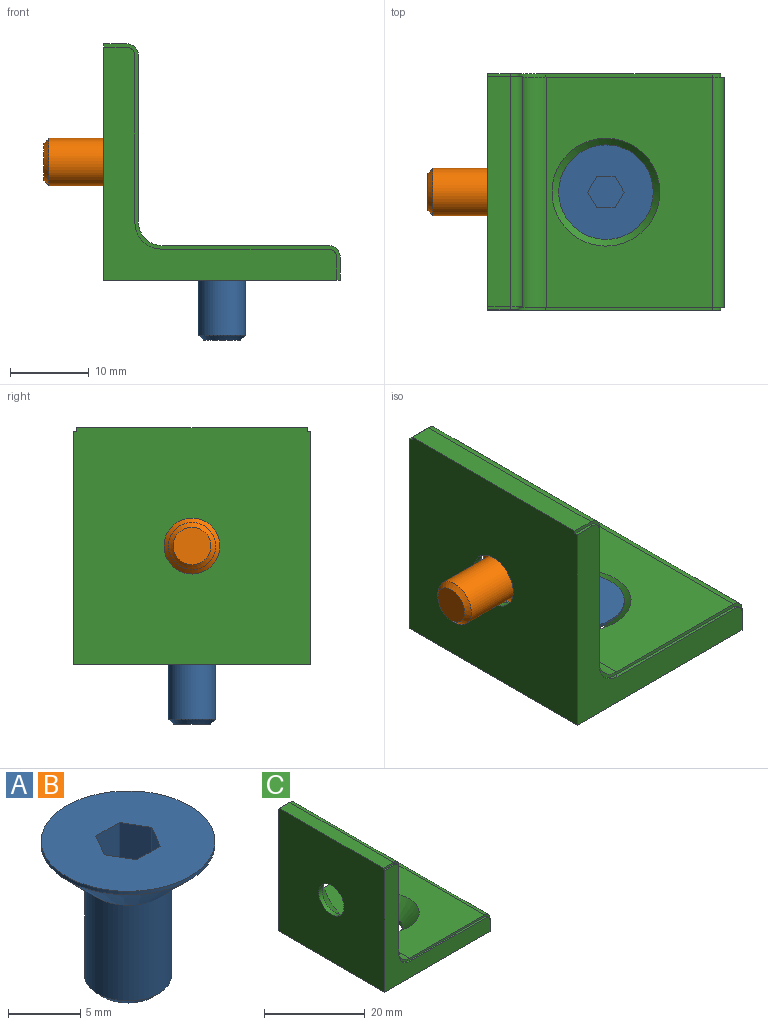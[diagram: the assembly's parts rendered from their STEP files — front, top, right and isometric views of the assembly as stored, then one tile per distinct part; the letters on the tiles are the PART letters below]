
ASSEMBLY  parts=3 mates=2
PART A: 13 faces, bbox 12x12x12 mm
  f0: cylinder r=6mm len=12mm, axis (0,0,-1), area 11.3mm2, adj f1,f9
  f1: cone r=3mm half-angle=45deg, axis (0,0,1), area 120mm2, adj f0,f2
  f2: cylinder r=3mm len=8.09mm, axis (0,0,-1), area 152.4mm2, adj f1,f3
  f3: cone r=1.5mm half-angle=45deg, axis (0,0,1), area 14.7mm2, adj f2,f12
  f4: plane 3.83x2mm, normal (0.87,0.5,0), area 8.9mm2, adj f6,f8,f9,f11
  f5: plane 3.83x2mm, normal (-0.87,-0.5,0), area 8.9mm2, adj f6,f7,f9,f10
  f6: plane 4.62x4mm, normal (0,0,1), area 13.9mm2, adj f4,f5,f7,f8,f10,f11
  f7: plane 3.83x2mm, normal (-0.87,0.5,0), area 8.9mm2, adj f5,f6,f9,f11
  f8: plane 3.83x2mm, normal (0.87,-0.5,0), area 8.9mm2, adj f4,f6,f9,f10
  f9: plane 12x12mm, normal (0,0,1), area 99.2mm2, adj f0,f4,f5,f7,f8,f10,f11
  f10: plane 3.83x2.31mm, normal (0,-1,0), area 8.9mm2, adj f5,f6,f8,f9
  f11: plane 3.83x2.31mm, normal (0,1,0), area 8.9mm2, adj f4,f6,f7,f9
  f12: plane 4.77x4.77mm, normal (0,0,-1), area 17.9mm2, adj f3
PART B: same geometry as A
PART C: 31 faces, bbox 30x30x30 mm
  f0: cone r=5.2mm half-angle=44.1deg, axis (0,0,1), area 154.8mm2, adj f1,f26
  f1: cylinder r=3.55mm len=7.1mm, axis (0,0,1), area 22.3mm2, adj f0,f29
  f2: cone r=5.2mm half-angle=44.1deg, axis (1,0,0), area 154.8mm2, adj f3,f24
  f3: cylinder r=3.55mm len=7.1mm, axis (1,0,0), area 22.3mm2, adj f2,f21
  f4: plane 21.15x0.4mm, normal (1,0,0), area 8.5mm2, adj f5,f8,f19,f30
  f5: cylinder r=1.1mm len=1.1mm, axis (0,-1,0), area 0.7mm2, adj f4,f9,f19,f30
  f6: cylinder r=1.1mm len=1.1mm, axis (0,-1,0), area 0.7mm2, adj f10,f17,f18,f20
  f7: cylinder r=3.4mm len=3.4mm, axis (0,-1,0), area 2.1mm2, adj f11,f17,f18,f20
  f8: cylinder r=3.4mm len=3.4mm, axis (0,-1,0), area 2.1mm2, adj f4,f12,f19,f30
  f9: plane 2.85x0.4mm, normal (0,0,1), area 1.1mm2, adj f5,f19,f21,f30
  f10: plane 2.85x0.4mm, normal (0,0,1), area 1.1mm2, adj f6,f18,f20,f21
  f11: plane 21.15x0.4mm, normal (0,0,1), area 8.5mm2, adj f7,f13,f18,f20
  f12: plane 21.15x0.4mm, normal (0,0,1), area 8.5mm2, adj f8,f14,f19,f30
  f13: cylinder r=1.1mm len=1.1mm, axis (0,-1,0), area 0.7mm2, adj f11,f15,f18,f20
  f14: cylinder r=1.1mm len=1.1mm, axis (0,-1,0), area 0.7mm2, adj f12,f16,f19,f30
  f15: plane 2.85x0.4mm, normal (1,0,0), area 1.1mm2, adj f13,f18,f20,f29
  f16: plane 2.85x0.4mm, normal (1,0,0), area 1.1mm2, adj f14,f19,f29,f30
  f17: plane 21.15x0.4mm, normal (1,0,0), area 8.5mm2, adj f6,f7,f18,f20
  f18: plane 29.6x29.6mm, normal (0,-1,0), area 220.2mm2, adj f6,f7,f10,f11,f13,f15,f17,f21
  f19: plane 29.6x29.6mm, normal (0,1,0), area 220.2mm2, adj f4,f5,f8,f9,f12,f14,f16,f21
  f20: plane 30x30mm, normal (0,-1,0), area 25.4mm2, adj f6,f7,f10,f11,f13,f15,f17,f21
  f21: plane 30x30mm, normal (-1,0,0), area 860.1mm2, adj f3,f9,f10,f18,f19,f20,f22,f29
  f22: plane 29.2x2.9mm, normal (0,0,1), area 84.7mm2, adj f20,f21,f23,f30
  f23: cylinder r=1.5mm len=29.2mm, axis (0,-1,0), area 68.8mm2, adj f20,f22,f24,f30
  f24: plane 29.2x21.1mm, normal (1,0,0), area 468.7mm2, adj f2,f20,f23,f25,f30
  f25: cylinder r=3mm len=29.2mm, axis (0,-1,0), area 137.6mm2, adj f20,f24,f26,f30
  f26: plane 29.2x21.1mm, normal (0,0,1), area 468.7mm2, adj f0,f20,f25,f27,f30
  f27: cylinder r=1.5mm len=29.2mm, axis (0,-1,0), area 68.8mm2, adj f20,f26,f28,f30
  f28: plane 29.2x2.9mm, normal (1,0,0), area 84.7mm2, adj f20,f27,f29,f30
  f29: plane 30x30mm, normal (0,0,-1), area 860.1mm2, adj f1,f15,f16,f18,f19,f20,f21,f28
  f30: plane 30x30mm, normal (0,1,0), area 25.4mm2, adj f4,f5,f8,f9,f12,f14,f16,f21
PLACE A t=(-16.74,-1.85,1.13)mm fixed
PLACE B rot(axis=(0,1,0),90deg) t=(-27.34,-1.85,11.73)mm fixed
PLACE C t=(-31.74,-1.85,-3.27)mm
MATE fastened B.f0 <-> C.f2  axis (1,0,0) through (-27.34,-1.85,11.73)mm
MATE fastened A.f0 <-> C.f0  axis (0,0,1) through (-16.74,-1.85,1.13)mm
